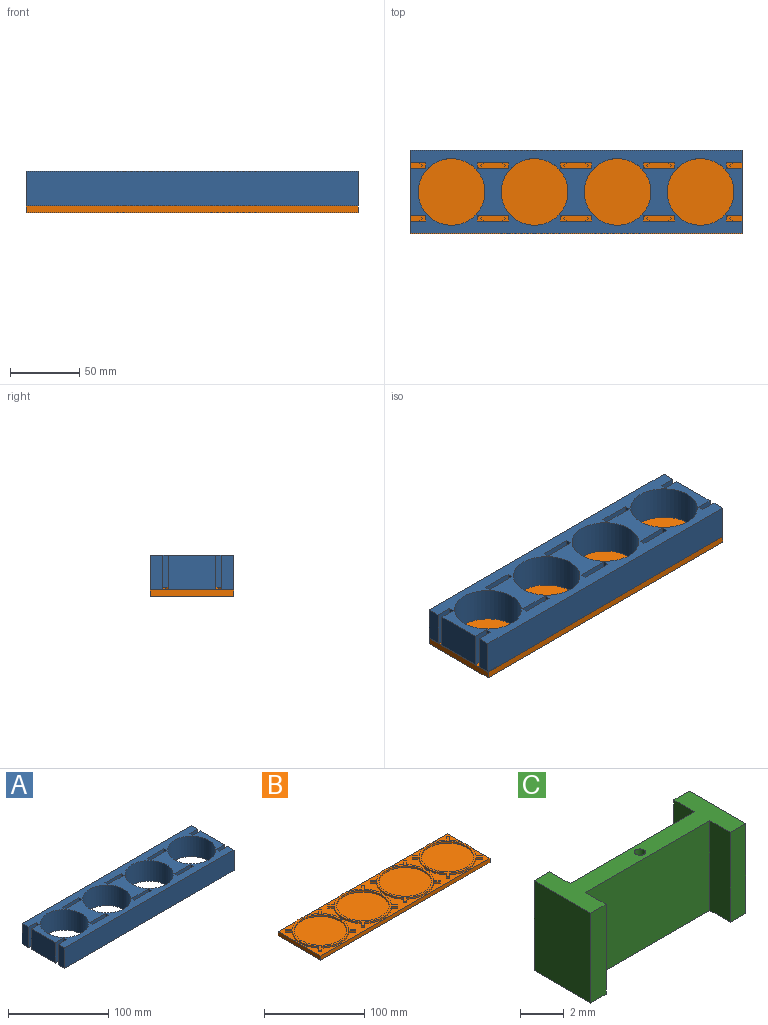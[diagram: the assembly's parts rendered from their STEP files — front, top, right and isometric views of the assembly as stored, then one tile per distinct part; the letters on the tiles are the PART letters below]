
ASSEMBLY  parts=3 mates=4
PART A: 50 faces, bbox 239x59.8x25 mm
  f0: plane 33.9x25mm, normal (1,0,0), area 847.6mm2, adj f2,f3,f13,f14
  f1: plane 25x8.92mm, normal (1,0,0), area 223.1mm2, adj f2,f3,f5,f11
  f2: plane 239x59.75mm, normal (0,0,1), area 6306mm2, adj f0,f1,f4,f5,f6,f7,f8,f9
  f3: plane 239x59.75mm, normal (0,0,-1), area 6306mm2, adj f0,f1,f4,f5,f6,f7,f8,f9
  f4: plane 25x8.92mm, normal (1,0,0), area 223.1mm2, adj f2,f3,f6,f16
  f5: plane 239x25mm, normal (0,1,0), area 5975mm2, adj f1,f2,f3,f40
  f6: plane 239x25mm, normal (0,-1,0), area 5975mm2, adj f2,f3,f4,f38
  f7: cylinder r=24mm len=48mm, axis (0,0,-1), area 3769.9mm2, adj f2,f3
  f8: plane 25x23mm, normal (0,-1,0), area 575mm2, adj f2,f3,f10,f24
  f9: plane 25x23mm, normal (0,1,0), area 575mm2, adj f2,f3,f10,f24
  f10: plane 25x4mm, normal (-1,0,0), area 100mm2, adj f2,f3,f8,f9
  f11: plane 25x11.5mm, normal (0,-1,0), area 287.5mm2, adj f1,f2,f3,f12
  f12: plane 25x4mm, normal (1,0,0), area 100mm2, adj f2,f3,f11,f13
  f13: plane 25x11.5mm, normal (0,1,0), area 287.5mm2, adj f0,f2,f3,f12
  f14: plane 25x11.5mm, normal (0,-1,0), area 287.5mm2, adj f0,f2,f3,f15
  f15: plane 25x4mm, normal (1,0,0), area 100mm2, adj f2,f3,f14,f16
  f16: plane 25x11.5mm, normal (0,1,0), area 287.5mm2, adj f2,f3,f4,f15
  f17: plane 25x23mm, normal (0,1,0), area 575mm2, adj f2,f3,f19,f25
  f18: plane 25x23mm, normal (0,-1,0), area 575mm2, adj f2,f3,f19,f25
  f19: plane 25x4mm, normal (-1,0,0), area 100mm2, adj f2,f3,f17,f18
  f20: cylinder r=24mm len=48mm, axis (0,0,-1), area 3769.9mm2, adj f2,f3
  f21: plane 25x23mm, normal (0,-1,0), area 575mm2, adj f2,f3,f23,f33
  f22: plane 25x23mm, normal (0,1,0), area 575mm2, adj f2,f3,f23,f33
  f23: plane 25x4mm, normal (-1,0,0), area 100mm2, adj f2,f3,f21,f22
  f24: plane 25x4mm, normal (1,0,0), area 100mm2, adj f2,f3,f8,f9
  f25: plane 25x4mm, normal (1,0,0), area 100mm2, adj f2,f3,f17,f18
  f26: plane 25x23mm, normal (0,1,0), area 575mm2, adj f2,f3,f28,f34
  f27: plane 25x23mm, normal (0,-1,0), area 575mm2, adj f2,f3,f28,f34
  f28: plane 25x4mm, normal (-1,0,0), area 100mm2, adj f2,f3,f26,f27
  f29: cylinder r=24mm len=48mm, axis (0,0,-1), area 3769.9mm2, adj f2,f3
  f30: plane 25x23mm, normal (0,-1,0), area 575mm2, adj f2,f3,f32,f45
  f31: plane 25x23mm, normal (0,1,0), area 575mm2, adj f2,f3,f32,f45
  f32: plane 25x4mm, normal (-1,0,0), area 100mm2, adj f2,f3,f30,f31
  f33: plane 25x4mm, normal (1,0,0), area 100mm2, adj f2,f3,f21,f22
  f34: plane 25x4mm, normal (1,0,0), area 100mm2, adj f2,f3,f26,f27
  f35: plane 25x23mm, normal (0,1,0), area 575mm2, adj f2,f3,f37,f46
  f36: plane 25x23mm, normal (0,-1,0), area 575mm2, adj f2,f3,f37,f46
  f37: plane 25x4mm, normal (-1,0,0), area 100mm2, adj f2,f3,f35,f36
  f38: plane 25x8.92mm, normal (-1,0,0), area 223.1mm2, adj f2,f3,f6,f47
  f39: plane 33.9x25mm, normal (-1,0,0), area 847.6mm2, adj f2,f3,f43,f48
  f40: plane 25x8.92mm, normal (-1,0,0), area 223.1mm2, adj f2,f3,f5,f42
  f41: cylinder r=24mm len=48mm, axis (0,0,-1), area 3769.9mm2, adj f2,f3
  f42: plane 25x11.5mm, normal (0,-1,0), area 287.5mm2, adj f2,f3,f40,f44
  f43: plane 25x11.5mm, normal (0,1,0), area 287.5mm2, adj f2,f3,f39,f44
  f44: plane 25x4mm, normal (-1,0,0), area 100mm2, adj f2,f3,f42,f43
  f45: plane 25x4mm, normal (1,0,0), area 100mm2, adj f2,f3,f30,f31
  f46: plane 25x4mm, normal (1,0,0), area 100mm2, adj f2,f3,f35,f36
  f47: plane 25x11.5mm, normal (0,1,0), area 287.5mm2, adj f2,f3,f38,f49
  f48: plane 25x11.5mm, normal (0,-1,0), area 287.5mm2, adj f2,f3,f39,f49
  f49: plane 25x4mm, normal (-1,0,0), area 100mm2, adj f2,f3,f47,f48
PART B: 85 faces, bbox 239x60x7 mm
  f0: plane 2.12x2.12mm, normal (0.71,0.71,0), area 6mm2, adj f1,f15,f17,f38
  f1: plane 4.62x4.62mm, normal (-0.71,0.71,0), area 13.1mm2, adj f0,f2,f17,f38
  f2: cylinder r=28.5mm len=38.13mm, axis (0,0,-1), area 83.5mm2, adj f1,f3,f17,f38
  f3: plane 4.62x4.62mm, normal (0.71,0.71,0), area 13.1mm2, adj f2,f4,f17,f38
  f4: plane 2.12x2.12mm, normal (-0.71,0.71,0), area 6mm2, adj f3,f5,f17,f38
  f5: plane 4.62x4.62mm, normal (-0.71,-0.71,0), area 13.1mm2, adj f4,f6,f17,f38
  f6: cylinder r=28.5mm len=38.13mm, axis (0,0,-1), area 83.5mm2, adj f5,f7,f17,f38
  f7: plane 4.62x4.62mm, normal (-0.71,0.71,0), area 13.1mm2, adj f6,f8,f17,f38
  f8: plane 2.12x2.12mm, normal (-0.71,-0.71,0), area 6mm2, adj f7,f9,f17,f38
  f9: plane 4.62x4.62mm, normal (0.71,-0.71,0), area 13.1mm2, adj f8,f10,f17,f38
  f10: cylinder r=28.5mm len=38.13mm, axis (0,0,-1), area 83.5mm2, adj f9,f11,f17,f38
  f11: plane 4.62x4.62mm, normal (-0.71,-0.71,0), area 13.1mm2, adj f10,f12,f17,f38
  f12: plane 2.12x2.12mm, normal (0.71,-0.71,0), area 6mm2, adj f11,f13,f17,f38
  f13: plane 4.62x4.62mm, normal (0.71,0.71,0), area 13.1mm2, adj f12,f14,f17,f38
  f14: cylinder r=28.5mm len=38.13mm, axis (0,0,-1), area 83.5mm2, adj f13,f15,f17,f38
  f15: plane 4.62x4.62mm, normal (0.71,-0.71,0), area 13.1mm2, adj f0,f14,f17,f38
  f16: cylinder r=26.25mm len=52.5mm, axis (0,0,-1), area 329.9mm2, adj f17,f18
  f17: plane 57x57mm, normal (0,0,1), area 465.2mm2, adj f0,f1,f2,f3,f4,f5,f6,f7
  f18: plane 52.5x52.5mm, normal (0,0,1), area 2164.8mm2, adj f16
  f19: plane 4.62x4.62mm, normal (0.71,0.71,0), area 13.1mm2, adj f20,f34,f36,f38
  f20: plane 2.12x2.12mm, normal (-0.71,0.71,0), area 6mm2, adj f19,f21,f36,f38
  f21: plane 4.62x4.62mm, normal (-0.71,-0.71,0), area 13.1mm2, adj f20,f22,f36,f38
  f22: cylinder r=28.5mm len=38.13mm, axis (0,0,-1), area 83.5mm2, adj f21,f23,f36,f38
  f23: plane 4.62x4.62mm, normal (-0.71,0.71,0), area 13.1mm2, adj f22,f24,f36,f38
  f24: plane 2.12x2.12mm, normal (-0.71,-0.71,0), area 6mm2, adj f23,f25,f36,f38
  f25: plane 4.62x4.62mm, normal (0.71,-0.71,0), area 13.1mm2, adj f24,f26,f36,f38
  f26: cylinder r=28.5mm len=38.13mm, axis (0,0,-1), area 83.5mm2, adj f25,f27,f36,f38
  f27: plane 4.62x4.62mm, normal (-0.71,-0.71,0), area 13.1mm2, adj f26,f28,f36,f38
  f28: plane 2.12x2.12mm, normal (0.71,-0.71,0), area 6mm2, adj f27,f29,f36,f38
  f29: plane 4.62x4.62mm, normal (0.71,0.71,0), area 13.1mm2, adj f28,f30,f36,f38
  f30: cylinder r=28.5mm len=38.13mm, axis (0,0,-1), area 83.5mm2, adj f29,f31,f36,f38
  f31: plane 4.62x4.62mm, normal (0.71,-0.71,0), area 13.1mm2, adj f30,f32,f36,f38
  f32: plane 2.12x2.12mm, normal (0.71,0.71,0), area 6mm2, adj f31,f33,f36,f38
  f33: plane 4.62x4.62mm, normal (-0.71,0.71,0), area 13.1mm2, adj f32,f34,f36,f38
  f34: cylinder r=28.5mm len=38.13mm, axis (0,0,-1), area 83.5mm2, adj f19,f33,f36,f38
  f35: cylinder r=26.25mm len=52.5mm, axis (0,0,-1), area 329.9mm2, adj f36,f37
  f36: plane 57x57mm, normal (0,0,1), area 465.2mm2, adj f19,f20,f21,f22,f23,f24,f25,f26
  f37: plane 52.5x52.5mm, normal (0,0,1), area 2164.8mm2, adj f35
  f38: plane 239x60mm, normal (0,0,1), area 3818mm2, adj f0,f1,f2,f3,f4,f5,f6,f7
  f39: plane 4.62x4.62mm, normal (0.71,0.71,0), area 13.1mm2, adj f38,f40,f54,f56
  f40: plane 2.12x2.12mm, normal (-0.71,0.71,0), area 6mm2, adj f38,f39,f41,f56
  f41: plane 4.62x4.62mm, normal (-0.71,-0.71,0), area 13.1mm2, adj f38,f40,f42,f56
  f42: cylinder r=28.5mm len=38.13mm, axis (0,0,-1), area 83.5mm2, adj f38,f41,f43,f56
  f43: plane 4.62x4.62mm, normal (-0.71,0.71,0), area 13.1mm2, adj f38,f42,f44,f56
  f44: plane 2.12x2.12mm, normal (-0.71,-0.71,0), area 6mm2, adj f38,f43,f45,f56
  f45: plane 4.62x4.62mm, normal (0.71,-0.71,0), area 13.1mm2, adj f38,f44,f46,f56
  f46: cylinder r=28.5mm len=38.13mm, axis (0,0,-1), area 83.5mm2, adj f38,f45,f47,f56
  f47: plane 4.62x4.62mm, normal (-0.71,-0.71,0), area 13.1mm2, adj f38,f46,f48,f56
  f48: plane 2.12x2.12mm, normal (0.71,-0.71,0), area 6mm2, adj f38,f47,f49,f56
  f49: plane 4.62x4.62mm, normal (0.71,0.71,0), area 13.1mm2, adj f38,f48,f50,f56
  f50: cylinder r=28.5mm len=38.13mm, axis (0,0,-1), area 83.5mm2, adj f38,f49,f51,f56
  f51: plane 4.62x4.62mm, normal (0.71,-0.71,0), area 13.1mm2, adj f38,f50,f52,f56
  f52: plane 2.12x2.12mm, normal (0.71,0.71,0), area 6mm2, adj f38,f51,f53,f56
  f53: plane 4.62x4.62mm, normal (-0.71,0.71,0), area 13.1mm2, adj f38,f52,f54,f56
  f54: cylinder r=28.5mm len=38.13mm, axis (0,0,-1), area 83.5mm2, adj f38,f39,f53,f56
  f55: cylinder r=26.25mm len=52.5mm, axis (0,0,-1), area 329.9mm2, adj f56,f57
  f56: plane 57x57mm, normal (0,0,1), area 465.2mm2, adj f39,f40,f41,f42,f43,f44,f45,f46
  f57: plane 52.5x52.5mm, normal (0,0,1), area 2164.8mm2, adj f55
  f58: plane 4.62x4.62mm, normal (0.71,0.71,0), area 13.1mm2, adj f38,f59,f73,f75
  f59: plane 2.12x2.12mm, normal (-0.71,0.71,0), area 6mm2, adj f38,f58,f60,f75
  f60: plane 4.62x4.62mm, normal (-0.71,-0.71,0), area 13.1mm2, adj f38,f59,f61,f75
  f61: cylinder r=28.5mm len=38.13mm, axis (0,0,-1), area 83.5mm2, adj f38,f60,f62,f75
  f62: plane 4.62x4.62mm, normal (-0.71,0.71,0), area 13.1mm2, adj f38,f61,f63,f75
  f63: plane 2.12x2.12mm, normal (-0.71,-0.71,0), area 6mm2, adj f38,f62,f64,f75
  f64: plane 4.62x4.62mm, normal (0.71,-0.71,0), area 13.1mm2, adj f38,f63,f65,f75
  f65: cylinder r=28.5mm len=38.13mm, axis (0,0,-1), area 83.5mm2, adj f38,f64,f66,f75
  f66: plane 4.62x4.62mm, normal (-0.71,-0.71,0), area 13.1mm2, adj f38,f65,f67,f75
  f67: plane 2.12x2.12mm, normal (0.71,-0.71,0), area 6mm2, adj f38,f66,f68,f75
  f68: plane 4.62x4.62mm, normal (0.71,0.71,0), area 13.1mm2, adj f38,f67,f69,f75
  f69: cylinder r=28.5mm len=38.13mm, axis (0,0,-1), area 83.5mm2, adj f38,f68,f70,f75
  f70: plane 4.62x4.62mm, normal (0.71,-0.71,0), area 13.1mm2, adj f38,f69,f71,f75
  f71: plane 2.12x2.12mm, normal (0.71,0.71,0), area 6mm2, adj f38,f70,f72,f75
  f72: plane 4.62x4.62mm, normal (-0.71,0.71,0), area 13.1mm2, adj f38,f71,f73,f75
  f73: cylinder r=28.5mm len=38.13mm, axis (0,0,-1), area 83.5mm2, adj f38,f58,f72,f75
  f74: cylinder r=26.25mm len=52.5mm, axis (0,0,-1), area 329.9mm2, adj f75,f76
  f75: plane 57x57mm, normal (0,0,1), area 465.2mm2, adj f58,f59,f60,f61,f62,f63,f64,f65
  f76: plane 52.5x52.5mm, normal (0,0,1), area 2164.8mm2, adj f74
  f77: plane 239x5mm, normal (0,1,0), area 1195mm2, adj f38,f78,f80,f81
  f78: plane 60x5mm, normal (-1,0,0), area 300mm2, adj f38,f77,f79,f81
  f79: plane 239x5mm, normal (0,-1,0), area 1195mm2, adj f38,f78,f80,f81
  f80: plane 60x5mm, normal (1,0,0), area 300mm2, adj f38,f77,f79,f81
  f81: plane 239x60mm, normal (0,0,-1), area 14337.6mm2, adj f77,f78,f79,f80,f82,f83,f84
  f82: cylinder r=0.5mm len=5mm, axis (0,0,1), area 15.7mm2, adj f38,f81
  f83: cylinder r=0.5mm len=5mm, axis (0,0,1), area 15.7mm2, adj f38,f81
  f84: cylinder r=0.5mm len=5mm, axis (0,0,1), area 15.7mm2, adj f38,f81
PART C: 15 faces, bbox 10x3.6x5 mm
  f0: cylinder r=0.25mm len=5mm, axis (0,0,-1), area 7.9mm2, adj f1,f2
  f1: plane 10x3.63mm, normal (0,0,1), area 15.1mm2, adj f0,f3,f4,f5,f6,f7,f8,f9
  f2: plane 10x3.63mm, normal (0,0,-1), area 15.1mm2, adj f0,f3,f4,f5,f6,f7,f8,f9
  f3: plane 8x5mm, normal (0,-1,0), area 40mm2, adj f1,f2,f5,f14
  f4: plane 8x5mm, normal (0,1,0), area 40mm2, adj f1,f2,f9,f10
  f5: plane 5x1.32mm, normal (-1,0,0), area 6.6mm2, adj f1,f2,f3,f6
  f6: plane 5x1mm, normal (0,-1,0), area 5mm2, adj f1,f2,f5,f7
  f7: plane 5x3.63mm, normal (1,0,0), area 18.2mm2, adj f1,f2,f6,f8
  f8: plane 5x1mm, normal (0,1,0), area 5mm2, adj f1,f2,f7,f9
  f9: plane 5x1.32mm, normal (-1,0,0), area 6.6mm2, adj f1,f2,f4,f8
  f10: plane 5x1.32mm, normal (1,0,0), area 6.6mm2, adj f1,f2,f4,f11
  f11: plane 5x1mm, normal (0,1,0), area 5mm2, adj f1,f2,f10,f12
  f12: plane 5x3.63mm, normal (-1,0,0), area 18.2mm2, adj f1,f2,f11,f13
  f13: plane 5x1mm, normal (0,-1,0), area 5mm2, adj f1,f2,f12,f14
  f14: plane 5x1.32mm, normal (1,0,0), area 6.6mm2, adj f1,f2,f3,f13
PLACE A t=(209.12,30,5)mm
PLACE B t=(0,60,5)mm
PLACE C rot(axis=(0,0,1),90deg) t=(179.25,30,5)mm
MATE parallel C.f12 <-> B.f79  axis (0,-1,0) through (179.25,25,7.5)mm
MATE cylindrical A.f7 <-> B.f2  axis (0,0,-1) through (209.12,30,5)mm
MATE revolute C.f0 <-> B.f82  axis (0,0,-1) through (179.25,30,5)mm
MATE planar B.f42 <-> A.f7  axis (0,0,1) through (89.63,30,5)mm
